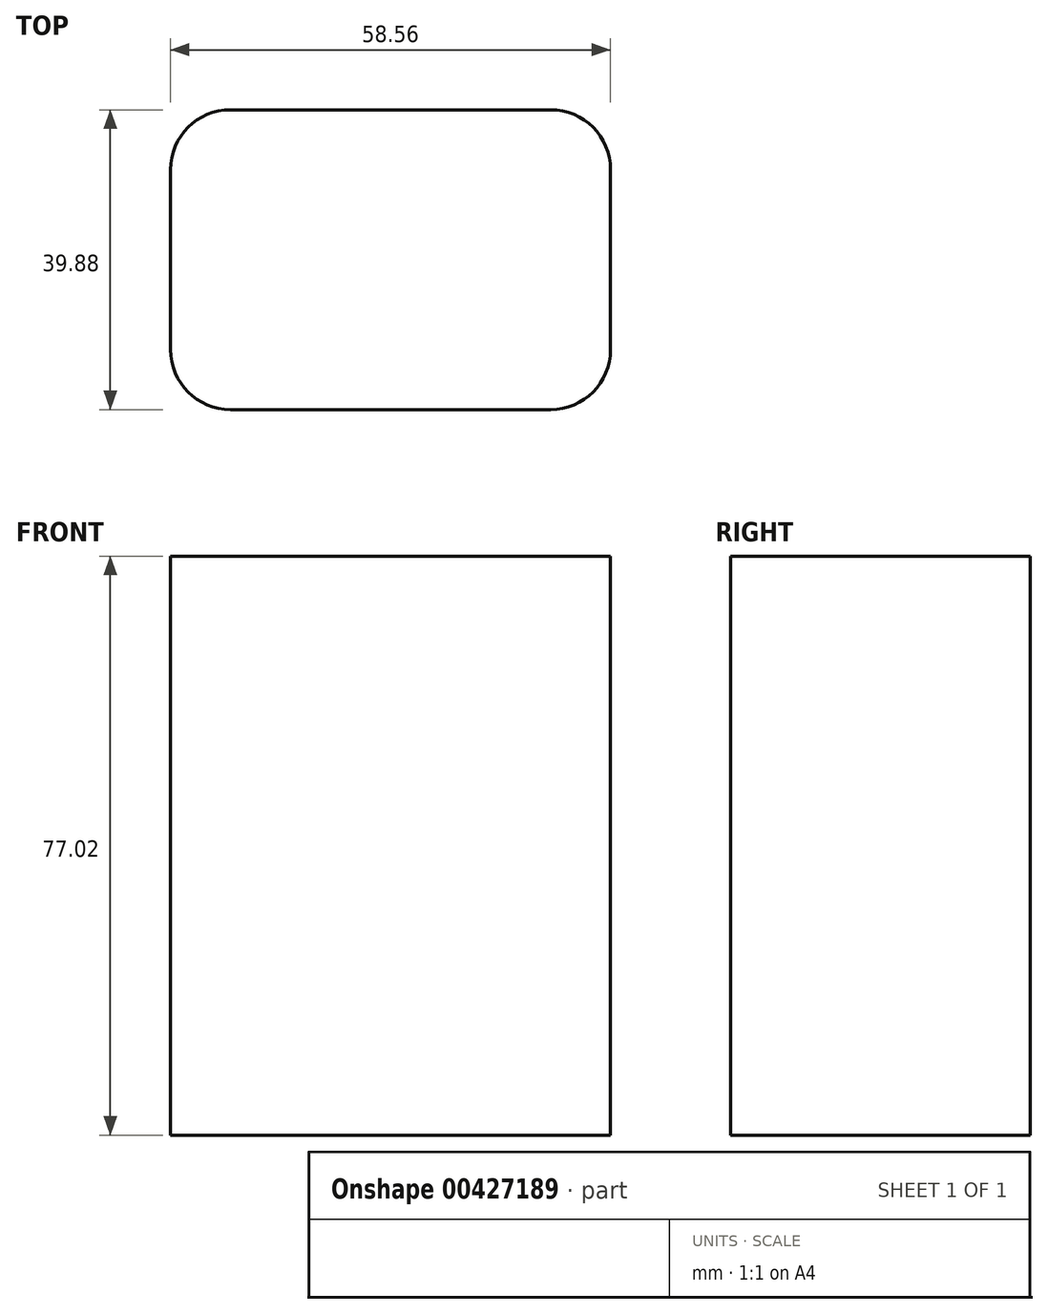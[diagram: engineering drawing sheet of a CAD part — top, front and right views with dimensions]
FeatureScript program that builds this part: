
annotation { "Feature Type Name" : "Feature", "Feature Type Description" : "" }
export const myFeature = defineFeature(function(context is Context, id is Id, definition is map)
    precondition{}
    {
        {
            var Q0;
            Q0=qCreatedBy(makeId("Front.planeOp"),FACE);
            var sketch = newSketch(context, id + "F0", { "sketchPlane" : qUnion([Q0])});
            skLineSegment(sketch, "E0.bottom", {"start": v(-28.72, 40.84) * mm, "end": v(29.84, 40.84) * mm});
            skLineSegment(sketch, "E0.top", {"start": v(-28.72, -36.18) * mm, "end": v(29.84, -36.18) * mm});
            skLineSegment(sketch, "E0.left", {"start": v(-28.72, 40.84) * mm, "end": v(-28.72, -36.18) * mm});
            skLineSegment(sketch, "E0.right", {"start": v(29.84, 40.84) * mm, "end": v(29.84, -36.18) * mm});
            skSolve(sketch);
        }
        {
            var Q0;
            Q0 = qSketchRegion(id + "F0", true);
            extrude(context, id + "F1", {"entities" : qUnion([Q0]), "depth" : 39.88 * mm});
        }
        {
            var Q0;
            Q0=makeQuery(id+"F1.opExtrude","CAP_EDGE",EDGE,{"disambiguationData":[OSD([sQuery(id+"F0.wireOp",EDGE,"E0.right")])],"isStart":false});
            var Q1;
            Q1=makeQuery(id+"F1.opExtrude","CAP_EDGE",EDGE,{"disambiguationData":[OSD([sQuery(id+"F0.wireOp",EDGE,"E0.left")])],"isStart":false});
            var Q2;
            Q2=makeQuery(id+"F1.opExtrude","CAP_EDGE",EDGE,{"disambiguationData":[OSD([sQuery(id+"F0.wireOp",EDGE,"E0.right")])],"isStart":true});
            var Q3;
            Q3=makeQuery(id+"F1.opExtrude","CAP_EDGE",EDGE,{"disambiguationData":[OSD([sQuery(id+"F0.wireOp",EDGE,"E0.left")])],"isStart":true});
            fillet(context, id + "F2", {"entities" : qUnion([Q0, Q1, Q2, Q3]), "radius" : 7.97 * mm, "tangentPropagation" : true, "allowEdgeOverflow" : false});
        }
        {
            var Q0;
            Q0=makeQuery(id+"F1.opExtrude","SWEPT_FACE",FACE,{"disambiguationData":[OSD([sQuery(id+"F0.wireOp",EDGE,"E0.bottom")])]});
            var sketch = newSketch(context, id + "F3", { "sketchPlane" : qUnion([Q0])});
            skLineSegment(sketch, "E1.bottom", {"start": v(-17.35, -6.32) * mm, "end": v(15.52, -6.32) * mm});
            skLineSegment(sketch, "E1.top", {"start": v(-17.35, -31.9) * mm, "end": v(15.52, -31.9) * mm});
            skLineSegment(sketch, "E1.left", {"start": v(-23.7, -12.67) * mm, "end": v(-23.7, -25.56) * mm});
            skLineSegment(sketch, "E1.right", {"start": v(21.87, -12.67) * mm, "end": v(21.87, -25.56) * mm});
            skPoint(sketch, "E2.visualSharp", {"position": v(-23.7, -6.32) * mm});
            skArc(sketch, "E2.filletArc", {"start": v(-17.35, -6.32) * mm, "mid": v(-21.84, -8.18) * mm, "end": v(-23.7, -12.67) * mm});
            skPoint(sketch, "E3.visualSharp", {"position": v(21.87, -6.32) * mm});
            skArc(sketch, "E3.filletArc", {"start": v(21.87, -12.67) * mm, "mid": v(20, -8.18) * mm, "end": v(15.52, -6.32) * mm});
            skPoint(sketch, "E4.visualSharp", {"position": v(21.87, -31.9) * mm});
            skArc(sketch, "E4.filletArc", {"start": v(15.52, -31.9) * mm, "mid": v(20, -30.05) * mm, "end": v(21.87, -25.56) * mm});
            skPoint(sketch, "E5.visualSharp", {"position": v(-23.7, -31.9) * mm});
            skArc(sketch, "E5.filletArc", {"start": v(-23.7, -25.56) * mm, "mid": v(-21.84, -30.05) * mm, "end": v(-17.35, -31.9) * mm});
            skCircle(sketch, "E6.cCircle", {"center": v(-13.24, -19.4) * mm, "radius": 4.48 * mm, "construction": true});
            skLineSegment(sketch, "E6.0", {"start": v(-10.66, -23.87) * mm, "end": v(-15.83, -23.87) * mm});
            skLineSegment(sketch, "E6.1", {"start": v(-15.83, -23.87) * mm, "end": v(-18.41, -19.4) * mm});
            skLineSegment(sketch, "E6.2", {"start": v(-18.41, -19.4) * mm, "end": v(-15.83, -14.92) * mm});
            skLineSegment(sketch, "E6.3", {"start": v(-15.83, -14.92) * mm, "end": v(-10.66, -14.92) * mm});
            skLineSegment(sketch, "E6.4", {"start": v(-10.66, -14.92) * mm, "end": v(-8.07, -19.4) * mm});
            skLineSegment(sketch, "E6.5", {"start": v(-8.07, -19.4) * mm, "end": v(-10.66, -23.87) * mm});
            skPoint(sketch, "E6.0.midPoint", {"position": v(-13.24, -23.87) * mm});
            skCircle(sketch, "E7", {"center": v(8.95, -19.2) * mm, "radius": 4.86 * mm});
            skCircle(sketch, "E8", {"center": v(-13.24, -19.4) * mm, "radius": 2.25 * mm});
            skCircle(sketch, "E9", {"center": v(8.95, -19.2) * mm, "radius": 1.87 * mm});
            skCircle(sketch, "E10", {"center": v(8.95, -19.2) * mm, "radius": 6.2 * mm});
            skSolve(sketch);
        }
        {
            var Q0;
            Q0=sQuery(id+"F3.wireOp",EDGE,"E6.3");
            var Q1;
            Q1=sQuery(id+"F3.wireOp",EDGE,"E6.2");
            var Q2;
            Q2=sQuery(id+"F3.wireOp",EDGE,"E6.1");
            var Q3;
            Q3=sQuery(id+"F3.wireOp",EDGE,"E6.0");
            var Q4;
            Q4=sQuery(id+"F3.wireOp",EDGE,"E6.5");
            var Q5;
            Q5=sQuery(id+"F3.wireOp",EDGE,"E6.4");
            var Q6;
            Q6=sQuery(id+"F3.wireOp",EDGE,"E7");
            var Q7;
            Q7=sQuery(id+"F3.wireOp",EDGE,"E1.bottom");
            extrude(context, id + "F4", {"bodyType" : ToolBodyType.SURFACE, "surfaceEntities" : qUnion([Q0, Q1, Q2, Q3, Q4, Q5, Q6, Q7]), "depth" : 2.54 * mm});
        }
        {
            var Q0;
            Q0=sQuery(id+"F3.wireOp",EDGE,"E1.bottom");
            var Q1;
            Q1=sQuery(id+"F3.wireOp",EDGE,"E2.filletArc");
            var Q2;
            Q2=sQuery(id+"F3.wireOp",EDGE,"E1.left");
            var Q3;
            Q3=sQuery(id+"F3.wireOp",EDGE,"E5.filletArc");
            var Q4;
            Q4=sQuery(id+"F3.wireOp",EDGE,"E1.top");
            var Q5;
            Q5=sQuery(id+"F3.wireOp",EDGE,"E4.filletArc");
            var Q6;
            Q6=sQuery(id+"F3.wireOp",EDGE,"E1.right");
            var Q7;
            Q7=sQuery(id+"F3.wireOp",EDGE,"E3.filletArc");
            extrude(context, id + "F5", {"bodyType" : ToolBodyType.SURFACE, "surfaceEntities" : qUnion([Q0, Q1, Q2, Q3, Q4, Q5, Q6, Q7]), "depth" : 1.78 * mm});
        }
        {
            var Q0;
            Q0 = qSketchRegion(id + "F3", true);
            extrude(context, id + "F6", {"entities" : qUnion([Q0]), "operationType" : NewBodyOperationType.ADD, "oppositeDirection" : true, "depth" : 0.76 * mm});
        }
        {
            var Q0;
            Q0=sQuery(id+"F3.wireOp",EDGE,"E9");
            extrude(context, id + "F7", {"bodyType" : ToolBodyType.SURFACE, "surfaceEntities" : qUnion([Q0]), "depth" : 1.52 * mm});
        }
        {
            var Q0;
            Q0=sQuery(id+"F3.wireOp",EDGE,"E8");
            extrude(context, id + "F8", {"bodyType" : ToolBodyType.SURFACE, "surfaceEntities" : qUnion([Q0]), "depth" : 1.78 * mm});
        }
        {
            var Q0;
            Q0=sQuery(id+"F3.wireOp",EDGE,"E10");
            extrude(context, id + "F9", {"bodyType" : ToolBodyType.SURFACE, "surfaceEntities" : qUnion([Q0]), "depth" : 0.25 * mm});
        }
    });
